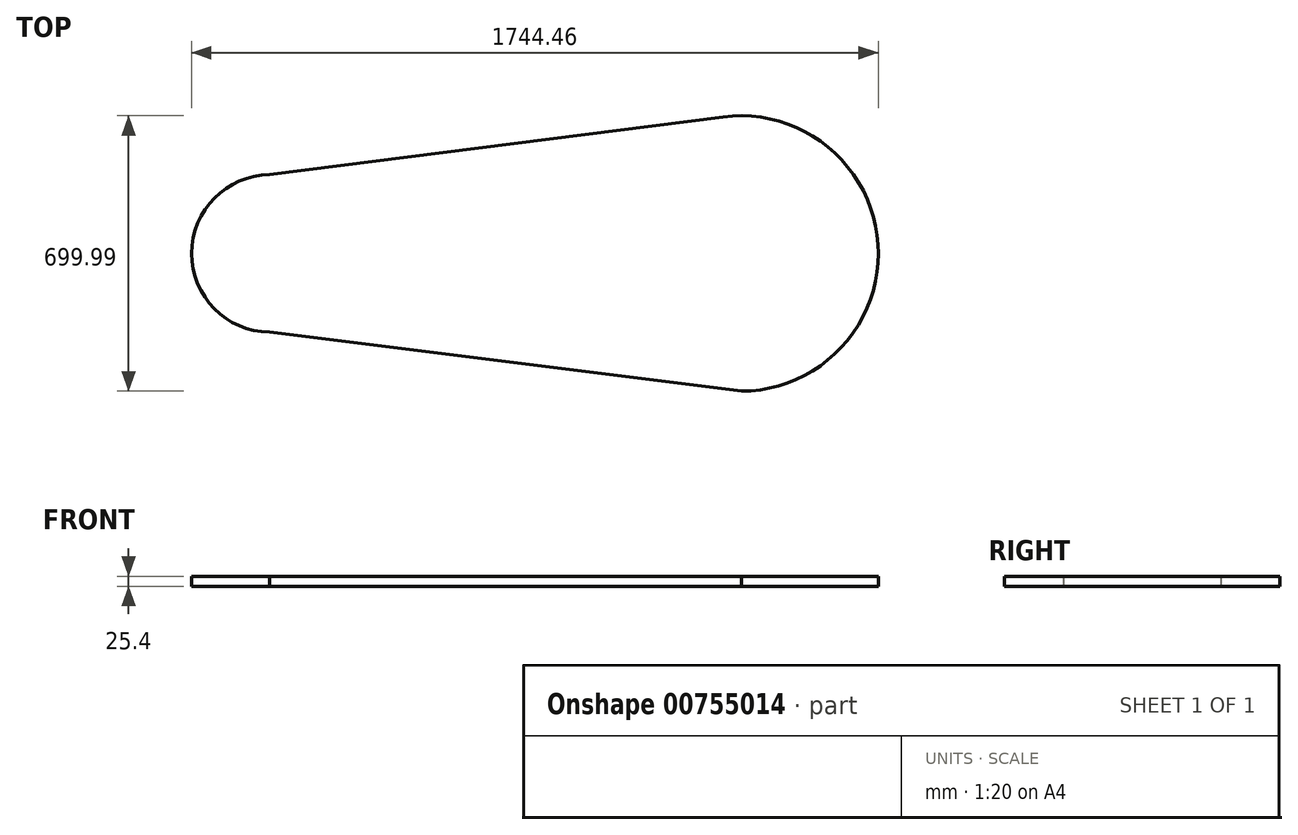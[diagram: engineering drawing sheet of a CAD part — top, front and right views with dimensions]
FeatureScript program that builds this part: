
annotation { "Feature Type Name" : "Feature", "Feature Type Description" : "" }
export const myFeature = defineFeature(function(context is Context, id is Id, definition is map)
    precondition{}
    {
        {
            var Q0;
            Q0=qCreatedBy(makeId("Top.planeOp"),FACE);
            var sketch = newSketch(context, id + "F0", { "sketchPlane" : qUnion([Q0])});
            skCircle(sketch, "E0", {"center": v(-558.02, 0) * mm, "radius": 200 * mm});
            skCircle(sketch, "E1", {"center": v(636.44, 0) * mm, "radius": 350 * mm});
            skLineSegment(sketch, "E2", {"start": v(-560.1, 199.99) * mm, "end": v(592.1, 347.18) * mm});
            skLineSegment(sketch, "E3", {"start": v(-560.44, -199.99) * mm, "end": v(638.57, -350) * mm});
            skSolve(sketch);
        }
        {
            var Q0;
            {var subQ0=sQuery(id+"F0.wireOp",EDGE,"E0");var subQ1=makeQuery(id+"F0.imprint","INTERSECT",VERTEX,{"derivedFrom":[subQ0,sQuery(id+"F0.wireOp",EDGE,"E2")]});Q0=makeQuery(id+"F0.imprint","IMPRINT",FACE,{"disambiguationData":[TD([[makeQuery(id+"F0.imprint","IMPRINT",EDGE,{"disambiguationData":[TD([[subQ1,-1.0]])],"derivedFrom":subQ0}),1.0]])]});}
            var Q1;
            {var subQ0=sQuery(id+"F0.wireOp",EDGE,"E2");Q1=makeQuery(id+"F0.imprint","IMPRINT",FACE,{"disambiguationData":[TD([[makeQuery(id+"F0.imprint","IMPRINT",EDGE,{"derivedFrom":subQ0}),-1.0]])]});}
            var Q2;
            {var subQ0=sQuery(id+"F0.wireOp",EDGE,"E1");var subQ1=makeQuery(id+"F0.imprint","INTERSECT",VERTEX,{"derivedFrom":[subQ0,sQuery(id+"F0.wireOp",EDGE,"E2")]});Q2=makeQuery(id+"F0.imprint","IMPRINT",FACE,{"disambiguationData":[TD([[makeQuery(id+"F0.imprint","IMPRINT",EDGE,{"disambiguationData":[TD([[subQ1,-1.0]])],"derivedFrom":subQ0}),1.0]])]});}
            extrude(context, id + "F1", {"entities" : qUnion([Q0, Q1, Q2]), "depth" : 25.4 * mm, "offsetDistance" : 25.4 * mm});
        }
    });
